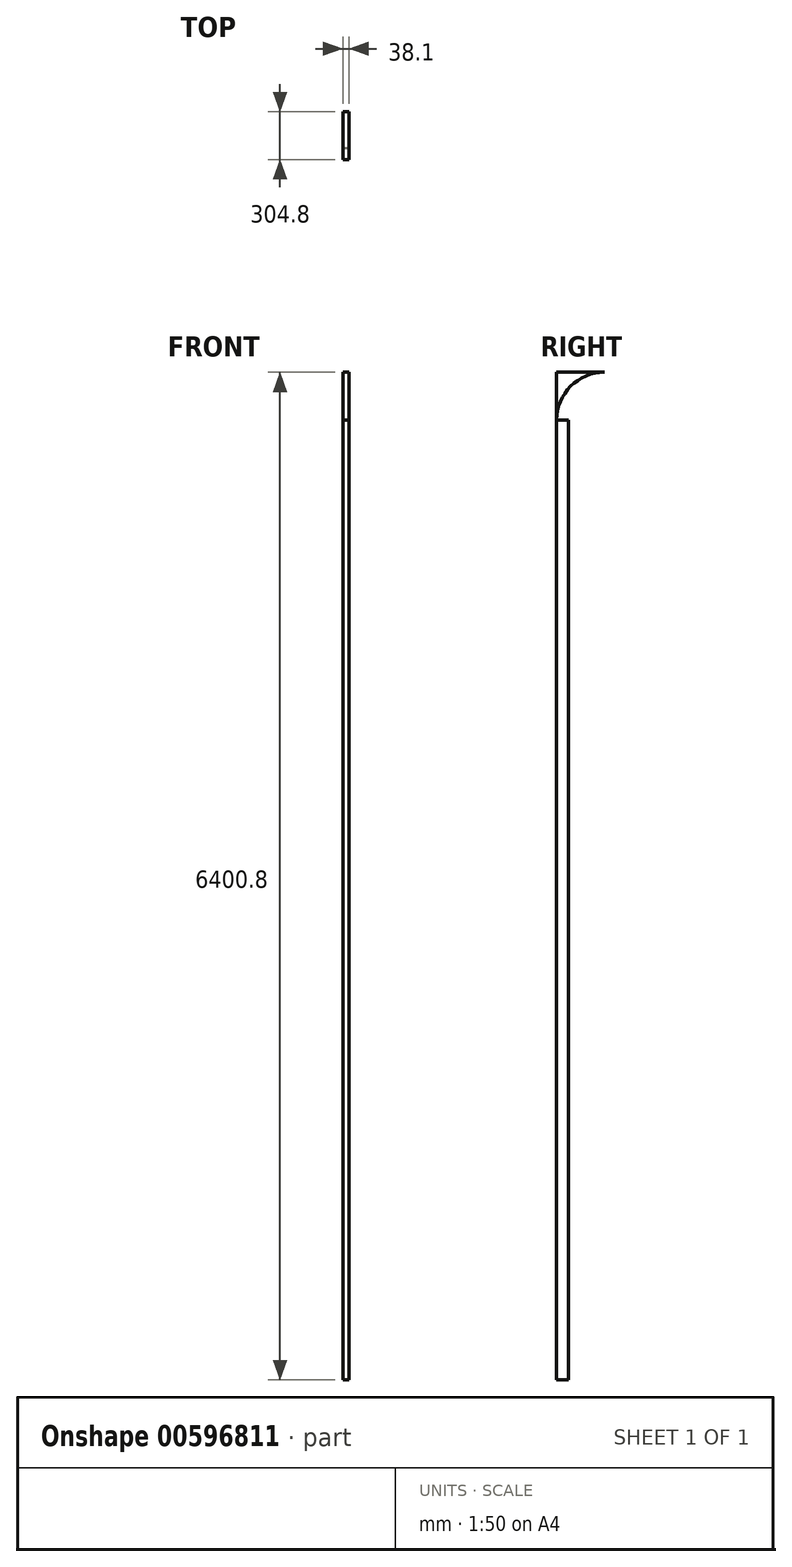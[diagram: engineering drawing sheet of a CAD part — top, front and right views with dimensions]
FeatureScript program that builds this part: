
annotation { "Feature Type Name" : "Feature", "Feature Type Description" : "" }
export const myFeature = defineFeature(function(context is Context, id is Id, definition is map)
    precondition{}
    {
        {
            var Q0;
            Q0=qCreatedBy(makeId("Top.planeOp"),FACE);
            var sketch = newSketch(context, id + "F0", { "sketchPlane" : qUnion([Q0])});
            skLineSegment(sketch, "E0.bottom", {"start": v(0, 0) * mm, "end": v(38.1, 0) * mm});
            skLineSegment(sketch, "E0.top", {"start": v(0, -76.2) * mm, "end": v(38.1, -76.2) * mm});
            skLineSegment(sketch, "E0.left", {"start": v(0, 0) * mm, "end": v(0, -76.2) * mm});
            skLineSegment(sketch, "E0.right", {"start": v(38.1, 0) * mm, "end": v(38.1, -76.2) * mm});
            skLineSegment(sketch, "E1", {"start": v(0, -3.81) * mm, "end": v(34.3, -3.81) * mm});
            skLineSegment(sketch, "E2", {"start": v(34.3, -3.81) * mm, "end": v(34.3, -72.4) * mm});
            skLineSegment(sketch, "E3", {"start": v(34.3, -72.4) * mm, "end": v(0, -72.4) * mm});
            skSolve(sketch);
        }
        {
            var Q0;
            {var subQ3=sQuery(id+"F0.wireOp",EDGE,"E0.bottom");Q0=makeQuery(id+"F0.imprint","IMPRINT",FACE,{"disambiguationData":[TD([[makeQuery(id+"F0.imprint","IMPRINT",EDGE,{"derivedFrom":subQ3}),-1.0]])]});}
            extrude(context, id + "F1", {"entities" : qUnion([Q0]), "depth" : 6096 * mm, "offsetDistance" : 25.4 * mm});
        }
        {
            var Q0;
            Q0=makeQuery(id+"F1.opExtrude","SWEPT_FACE",FACE,{"disambiguationData":[OSD([sQuery(id+"F0.wireOp",EDGE,"E0.right")])]});
            var sketch = newSketch(context, id + "F2", { "sketchPlane" : qUnion([Q0])});
            skLineSegment(sketch, "E4.bottom", {"start": v(-76.2, 6096) * mm, "end": v(228.6, 6096) * mm});
            skLineSegment(sketch, "E4.top", {"start": v(-76.2, 6400.8) * mm, "end": v(228.6, 6400.8) * mm});
            skLineSegment(sketch, "E4.left", {"start": v(-76.2, 6096) * mm, "end": v(-76.2, 6400.8) * mm});
            skLineSegment(sketch, "E4.right", {"start": v(228.6, 6096) * mm, "end": v(228.6, 6400.8) * mm});
            skArc(sketch, "E5", {"start": v(-76.2, 6096) * mm, "mid": v(13.07, 6311.53) * mm, "end": v(228.6, 6400.8) * mm});
            skArc(sketch, "E6", {"start": v(0, 6096) * mm, "mid": v(66.96, 6257.64) * mm, "end": v(228.6, 6324.6) * mm});
            skSolve(sketch);
        }
        {
            var Q0;
            {var subQ3=sQuery(id+"F2.wireOp",EDGE,"E5");Q0=makeQuery(id+"F2.imprint","IMPRINT",FACE,{"disambiguationData":[TD([[makeQuery(id+"F2.imprint","IMPRINT",EDGE,{"derivedFrom":subQ3}),-1.0]])]});}
            extrude(context, id + "F3", {"entities" : qUnion([Q0]), "operationType" : NewBodyOperationType.ADD, "oppositeDirection" : true, "depth" : 38.1 * mm, "offsetDistance" : 25.4 * mm});
        }
    });
